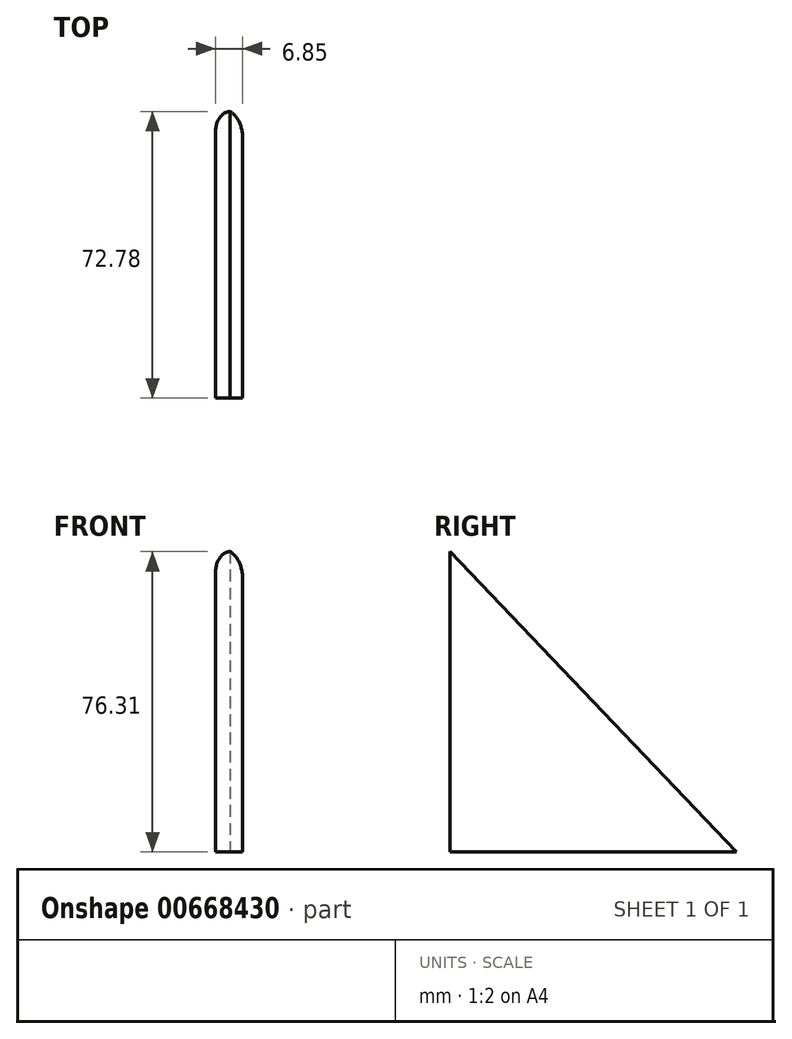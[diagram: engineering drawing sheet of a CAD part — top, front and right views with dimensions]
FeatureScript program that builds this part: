
annotation { "Feature Type Name" : "Feature", "Feature Type Description" : "" }
export const myFeature = defineFeature(function(context is Context, id is Id, definition is map)
    precondition{}
    {
        {
            var Q0;
            Q0=qCreatedBy(makeId("Right.planeOp"),FACE);
            var sketch = newSketch(context, id + "F0", { "sketchPlane" : qUnion([Q0])});
            skLineSegment(sketch, "E0", {"start": v(0, 76.31) * mm, "end": v(72.78, 0) * mm});
            skLineSegment(sketch, "E1", {"start": v(72.78, 0) * mm, "end": v(0, 0) * mm});
            skLineSegment(sketch, "E2", {"start": v(0, 0) * mm, "end": v(0, 76.31) * mm});
            skSolve(sketch);
        }
        {
            var Q0;
            Q0=makeQuery(id+"F0.imprint","IMPRINT",FACE,{"disambiguationData":[TD([[makeQuery(id+"F0.imprint","IMPRINT",EDGE,{"derivedFrom":sQuery(id+"F0.wireOp",EDGE,"E0")}),-1.0]])]});
            extrude(context, id + "F1", {"entities" : qUnion([Q0]), "depth" : 4.06 * mm, "offsetDistance" : 25.4 * mm});
        }
        {
            var Q0;
            Q0=makeQuery(id+"F1.opExtrude","CAP_FACE",FACE,{"disambiguationData":[OSD([sQuery(id+"F0.wireOp",EDGE,"E0"),sQuery(id+"F0.wireOp",EDGE,"E1"),sQuery(id+"F0.wireOp",EDGE,"E2")])],"isStart":true});
            extrude(context, id + "F2", {"entities" : qUnion([Q0]), "operationType" : NewBodyOperationType.ADD, "depth" : 2.8 * mm, "offsetDistance" : 25.4 * mm});
        }
        {
            var Q0;
            Q0=makeQuery(id+"F2.opExtrude","CAP_EDGE",EDGE,{"disambiguationData":[OSD([sQuery(id+"F0.wireOp",EDGE,"E0")])],"isStart":false});
            fillet(context, id + "F3", {"entities" : qUnion([Q0]), "radius" : 3.68 * mm, "tangentPropagation" : true, "allowEdgeOverflow" : false});
        }
        {
            var Q0;
            Q0=makeQuery(id+"F1.opExtrude","CAP_EDGE",EDGE,{"disambiguationData":[OSD([sQuery(id+"F0.wireOp",EDGE,"E0")])],"isStart":false});
            fillet(context, id + "F4", {"entities" : qUnion([Q0]), "radius" : 5.08 * mm, "tangentPropagation" : true, "allowEdgeOverflow" : false});
        }
    });
